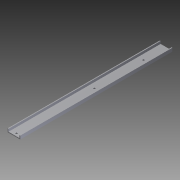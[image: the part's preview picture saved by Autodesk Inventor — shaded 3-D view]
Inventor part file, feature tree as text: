
AUTODESK INVENTOR PART (.ipt)
format: ipt  version: 2011 (Build 150239000, 239)  size: 130,048 bytes
history: native  units: in
note: dims shown in document units (in); Inventor stores cm internally (conversion verified against a paired STEP export)
features: extrude x5, sketch x5
ambient origin geometry x8: Origin, YZ Plane, XZ Plane, XY Plane, X Axis, Y Axis, Z Axis, Center Point
bodies: Solid1 (feature_tree)
feature tree (10):
  extrude  "Extrusion1"  Depth=0.374in
  extrude  "Extrusion2"  Depth=17.7165in TaperAngle=0.0deg
  extrude  "Extrusion3"  Depth=0.1693in
  extrude  "Extrusion4"  Depth=13.8583in
  extrude  "Extrusion5"  Depth=16.5in TaperAngle=0.0deg
  sketch  "Sketch1"  dims[d0=1.3898in d1=0.374in]
  sketch  "Sketch2"  dims[d2=45.0deg d3=17.7165in d4=0.0in]
  sketch  "Sketch3"  dims[d5=1.0236in d6=0.1693in]
  sketch  "Sketch4"  dims[d7=15.1181in d8=13.8583in]
  sketch  "Sketch5"  dims[d9=17.7165in d10=0.0in d11=16.5in d12=0.0in d13=16.7812in d14=0.0in d15=2.49in d16=0.185in d17=8.0in d18=0.0925in d19=16.5in d20=16.7812in d21=0.0in]
